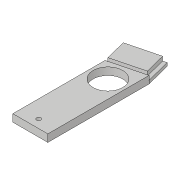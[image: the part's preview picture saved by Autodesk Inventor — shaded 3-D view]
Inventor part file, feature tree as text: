
AUTODESK INVENTOR PART (.ipt)
format: ipt  version: 2018.3 (Build 223284000, 284)  size: 121,856 bytes
history: native  units: in
note: dims shown in document units (in); Inventor stores cm internally (conversion verified against a paired STEP export)
features: extrude x4, sketch x3
ambient origin geometry x8: Origin, YZ Plane, XZ Plane, XY Plane, X Axis, Y Axis, Z Axis, Center Point
bodies: Solid1 (feature_tree)
feature tree (7):
  extrude  "Extrusion1"  Depth=0.125in TaperAngle=0.0deg
  extrude  "Extrusion2"  Depth=0.75in
  extrude  "Extrusion3"  Depth=0.75in
  extrude  "Extrusion4"  Depth=1.0429in
  sketch  "Sketch1"  dims[d4=0.88in d5=0.221in d6=0.0in d13=0.125in d14=0.0in]
  sketch  "Sketch2"  dims[d18=0.125in d19=0.0in d24=0.75in]
  sketch  "Sketch4"  dims[d25=2.75in d26=0.75in d28=1.0429in d29=0.5215in d30=0.126in d31=0.5215in d32=0.25in d33=1.0in d34=0.0in d35=2.3125in d36=0.52in d37=0.119in d38=0.1105in]
